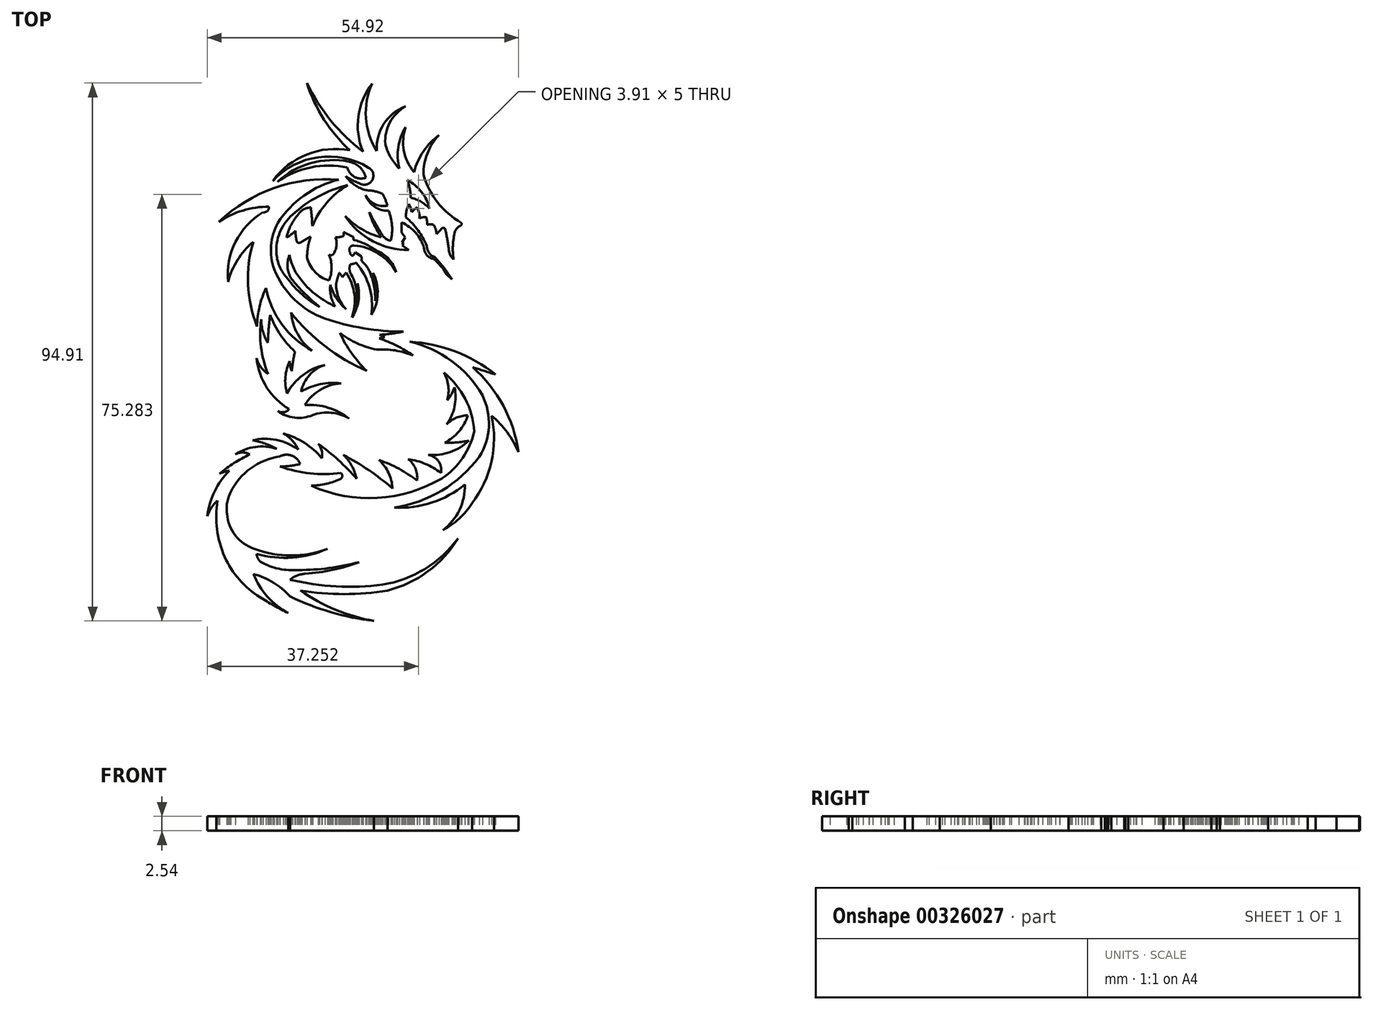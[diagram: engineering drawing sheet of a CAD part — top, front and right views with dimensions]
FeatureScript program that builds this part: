
annotation { "Feature Type Name" : "Feature", "Feature Type Description" : "" }
export const myFeature = defineFeature(function(context is Context, id is Id, definition is map)
    precondition{}
    {
        {
            var Q0;
            Q0=qCreatedBy(makeId("Top.planeOp"),FACE);
            var sketch = newSketch(context, id + "F0", { "sketchPlane" : qUnion([Q0])});
            skArc(sketch, "E0", {"start": v(-30.65, 39.22) * mm, "mid": v(-28.15, 34.33) * mm, "end": v(-23.98, 30.75) * mm});
            skArc(sketch, "E1", {"start": v(-27.91, 46.24) * mm, "mid": v(-29.97, 43) * mm, "end": v(-30.65, 39.22) * mm});
            skArc(sketch, "E2", {"start": v(-27.91, 46.24) * mm, "mid": v(-30.67, 43.35) * mm, "end": v(-32.32, 39.7) * mm});
            skArc(sketch, "E3", {"start": v(-33.8, 47.63) * mm, "mid": v(-34.11, 43.47) * mm, "end": v(-32.32, 39.7) * mm});
            skArc(sketch, "E4", {"start": v(-33.8, 47.63) * mm, "mid": v(-35.12, 44.08) * mm, "end": v(-34.92, 40.3) * mm});
            skArc(sketch, "E5", {"start": v(-37.4, 44.6) * mm, "mid": v(-36.44, 42.3) * mm, "end": v(-34.92, 40.3) * mm});
            skArc(sketch, "E6", {"start": v(-33.82, 51.28) * mm, "mid": v(-36.58, 48.47) * mm, "end": v(-37.4, 44.6) * mm});
            skArc(sketch, "E7", {"start": v(-33.82, 51.28) * mm, "mid": v(-37.67, 48.18) * mm, "end": v(-38.9, 43.4) * mm});
            skArc(sketch, "E8", {"start": v(-39.73, 55.3) * mm, "mid": v(-40.83, 49.25) * mm, "end": v(-38.9, 43.4) * mm});
            skArc(sketch, "E9", {"start": v(-39.73, 55.3) * mm, "mid": v(-42.15, 49.52) * mm, "end": v(-41.34, 43.3) * mm});
            skArc(sketch, "E10", {"start": v(-51.25, 55.4) * mm, "mid": v(-47, 48.77) * mm, "end": v(-41.34, 43.3) * mm});
            skArc(sketch, "E11", {"start": v(-51.25, 55.4) * mm, "mid": v(-48.2, 48.97) * mm, "end": v(-43.64, 43.52) * mm});
            skArc(sketch, "E12", {"start": v(-43.64, 43.52) * mm, "mid": v(-51.25, 42.81) * mm, "end": v(-57.28, 38.12) * mm});
            skArc(sketch, "E13", {"start": v(-40.35, 40.47) * mm, "mid": v(-49.23, 42.31) * mm, "end": v(-57.28, 38.12) * mm});
            skArc(sketch, "E14", {"start": v(-41.33, 37.48) * mm, "mid": v(-39.58, 38.56) * mm, "end": v(-40.35, 40.47) * mm});
            skArc(sketch, "E15", {"start": v(-44.38, 38.98) * mm, "mid": v(-42.91, 38.11) * mm, "end": v(-41.33, 37.48) * mm});
            skArc(sketch, "E16", {"start": v(-44.38, 38.98) * mm, "mid": v(-42.8, 37.4) * mm, "end": v(-40.77, 36.48) * mm});
            skArc(sketch, "E17", {"start": v(-37.91, 35.86) * mm, "mid": v(-39.31, 36.3) * mm, "end": v(-40.77, 36.48) * mm});
            skArc(sketch, "E18", {"start": v(-37.01, 33.75) * mm, "mid": v(-37.4, 34.83) * mm, "end": v(-37.91, 35.86) * mm});
            skArc(sketch, "E19", {"start": v(-40.85, 35.6) * mm, "mid": v(-39.24, 34.04) * mm, "end": v(-37.01, 33.75) * mm});
            skArc(sketch, "E20", {"start": v(-40.85, 35.6) * mm, "mid": v(-39.3, 33.56) * mm, "end": v(-36.83, 32.89) * mm});
            skArc(sketch, "E21", {"start": v(-44.1, 40.51) * mm, "mid": v(-50.54, 40.52) * mm, "end": v(-56.45, 37.97) * mm});
            skArc(sketch, "E22", {"start": v(-44.1, 40.51) * mm, "mid": v(-42.88, 38.87) * mm, "end": v(-40.83, 38.7) * mm});
            skArc(sketch, "E23", {"start": v(-40.83, 38.7) * mm, "mid": v(-41.92, 40.55) * mm, "end": v(-43.82, 41.54) * mm});
            skArc(sketch, "E24", {"start": v(-43.82, 41.54) * mm, "mid": v(-50.56, 41.26) * mm, "end": v(-56.45, 37.97) * mm});
            skArc(sketch, "E25", {"start": v(-36.45, 27.58) * mm, "mid": v(-36.2, 30.27) * mm, "end": v(-36.83, 32.89) * mm});
            skArc(sketch, "E26", {"start": v(-37.87, 28.52) * mm, "mid": v(-37.26, 27.9) * mm, "end": v(-36.45, 27.58) * mm});
            skArc(sketch, "E27", {"start": v(-40.23, 32.6) * mm, "mid": v(-39.08, 30.55) * mm, "end": v(-37.87, 28.52) * mm});
            skArc(sketch, "E28", {"start": v(-40.23, 32.6) * mm, "mid": v(-39.32, 30.32) * mm, "end": v(-38.12, 28.17) * mm});
            skArc(sketch, "E29", {"start": v(-44.48, 31.94) * mm, "mid": v(-41.56, 29.61) * mm, "end": v(-38.12, 28.17) * mm});
            skArc(sketch, "E30", {"start": v(-44.48, 31.94) * mm, "mid": v(-39.63, 27.52) * mm, "end": v(-33.25, 25.95) * mm});
            skLineSegment(sketch, "E31", {"start": v(-33.25, 25.95) * mm, "end": v(-34.39, 26.7) * mm});
            skLineSegment(sketch, "E32", {"start": v(-34.39, 26.7) * mm, "end": v(-34.17, 27.04) * mm});
            skLineSegment(sketch, "E33", {"start": v(-34.17, 27.04) * mm, "end": v(-34.49, 27.25) * mm});
            skLineSegment(sketch, "E34", {"start": v(-34.49, 27.25) * mm, "end": v(-33.88, 28.16) * mm});
            skLineSegment(sketch, "E35", {"start": v(-33.88, 28.16) * mm, "end": v(-34.5, 28.99) * mm});
            skLineSegment(sketch, "E36", {"start": v(-34.5, 28.99) * mm, "end": v(-34.5, 30.8) * mm});
            skArc(sketch, "E37", {"start": v(-30.56, 26.27) * mm, "mid": v(-32.03, 28.98) * mm, "end": v(-34.5, 30.8) * mm});
            skArc(sketch, "E38", {"start": v(-30.56, 26.27) * mm, "mid": v(-30.05, 25.03) * mm, "end": v(-28.88, 24.37) * mm});
            skArc(sketch, "E39", {"start": v(-26.66, 21.73) * mm, "mid": v(-27.64, 23.16) * mm, "end": v(-28.88, 24.37) * mm});
            skLineSegment(sketch, "E40", {"start": v(-26.66, 21.73) * mm, "end": v(-25.6, 20.73) * mm});
            skArc(sketch, "E41", {"start": v(-25.6, 20.73) * mm, "mid": v(-27.04, 22.77) * mm, "end": v(-28.66, 24.67) * mm});
            skArc(sketch, "E42", {"start": v(-30.06, 26.64) * mm, "mid": v(-29.68, 25.43) * mm, "end": v(-28.66, 24.67) * mm});
            skArc(sketch, "E43", {"start": v(-30.06, 26.64) * mm, "mid": v(-31.62, 29.41) * mm, "end": v(-33.8, 31.73) * mm});
            skArc(sketch, "E44", {"start": v(-33.24, 34.08) * mm, "mid": v(-33.64, 32.93) * mm, "end": v(-33.8, 31.73) * mm});
            skArc(sketch, "E45", {"start": v(-32.75, 32.61) * mm, "mid": v(-32.92, 33.37) * mm, "end": v(-33.24, 34.08) * mm});
            skArc(sketch, "E46", {"start": v(-31.8, 33.49) * mm, "mid": v(-32.29, 33.06) * mm, "end": v(-32.75, 32.61) * mm});
            skArc(sketch, "E47", {"start": v(-31.35, 31.52) * mm, "mid": v(-31.44, 32.54) * mm, "end": v(-31.8, 33.49) * mm});
            skArc(sketch, "E48", {"start": v(-30.2, 31.73) * mm, "mid": v(-30.8, 31.7) * mm, "end": v(-31.35, 31.52) * mm});
            skArc(sketch, "E49", {"start": v(-30.04, 30.38) * mm, "mid": v(-30.04, 31.07) * mm, "end": v(-30.2, 31.73) * mm});
            skArc(sketch, "E50", {"start": v(-28.88, 30.38) * mm, "mid": v(-29.46, 30.48) * mm, "end": v(-30.04, 30.38) * mm});
            skArc(sketch, "E51", {"start": v(-28.37, 28.76) * mm, "mid": v(-28.5, 29.61) * mm, "end": v(-28.88, 30.38) * mm});
            skArc(sketch, "E52", {"start": v(-28.37, 28.76) * mm, "mid": v(-27.87, 29.27) * mm, "end": v(-27.38, 29.8) * mm});
            skArc(sketch, "E53", {"start": v(-26.81, 29.56) * mm, "mid": v(-27.04, 29.83) * mm, "end": v(-27.38, 29.8) * mm});
            skArc(sketch, "E54", {"start": v(-26.23, 26.32) * mm, "mid": v(-26.48, 27.95) * mm, "end": v(-26.81, 29.56) * mm});
            skArc(sketch, "E55", {"start": v(-26.23, 26.32) * mm, "mid": v(-25.99, 25.22) * mm, "end": v(-25.35, 24.28) * mm});
            skArc(sketch, "E56", {"start": v(-25.1, 29.19) * mm, "mid": v(-25.46, 26.74) * mm, "end": v(-25.35, 24.28) * mm});
            skArc(sketch, "E57", {"start": v(-24.27, 30.17) * mm, "mid": v(-24.76, 29.74) * mm, "end": v(-25.1, 29.19) * mm});
            skArc(sketch, "E58", {"start": v(-24.27, 30.17) * mm, "mid": v(-23.97, 30.38) * mm, "end": v(-23.98, 30.75) * mm});
            skArc(sketch, "E59", {"start": v(-29.6, 33.27) * mm, "mid": v(-31.01, 36.2) * mm, "end": v(-33.51, 38.27) * mm});
            skArc(sketch, "E60", {"start": v(-29.6, 33.27) * mm, "mid": v(-31.1, 34.46) * mm, "end": v(-32.9, 35.15) * mm});
            skArc(sketch, "E61", {"start": v(-32.9, 35.15) * mm, "mid": v(-33.08, 36.73) * mm, "end": v(-33.51, 38.27) * mm});
            skArc(sketch, "E62", {"start": v(-44.07, 37.38) * mm, "mid": v(-49.23, 35.39) * mm, "end": v(-53.76, 32.2) * mm});
            skArc(sketch, "E63", {"start": v(-53.76, 32.2) * mm, "mid": v(-56.03, 29.04) * mm, "end": v(-56.6, 25.2) * mm});
            skArc(sketch, "E64", {"start": v(-56.6, 25.2) * mm, "mid": v(-55.99, 22.86) * mm, "end": v(-54.62, 20.88) * mm});
            skArc(sketch, "E65", {"start": v(-54.62, 20.88) * mm, "mid": v(-52.08, 18.07) * mm, "end": v(-48.97, 15.88) * mm});
            skArc(sketch, "E66", {"start": v(-54, 20.88) * mm, "mid": v(-51.62, 18.24) * mm, "end": v(-48.97, 15.88) * mm});
            skArc(sketch, "E67", {"start": v(-54.31, 25.05) * mm, "mid": v(-54.65, 22.93) * mm, "end": v(-54, 20.88) * mm});
            skArc(sketch, "E68", {"start": v(-54.31, 25.05) * mm, "mid": v(-53.52, 22.62) * mm, "end": v(-52.11, 20.49) * mm});
            skArc(sketch, "E69", {"start": v(-52.11, 20.49) * mm, "mid": v(-49.47, 17.9) * mm, "end": v(-46.27, 16.02) * mm});
            skArc(sketch, "E70", {"start": v(-47.1, 19.82) * mm, "mid": v(-47, 17.85) * mm, "end": v(-46.27, 16.02) * mm});
            skArc(sketch, "E71", {"start": v(-47.1, 19.82) * mm, "mid": v(-46.04, 17.46) * mm, "end": v(-44.33, 15.5) * mm});
            skArc(sketch, "E72", {"start": v(-46.1, 19.91) * mm, "mid": v(-45.63, 17.54) * mm, "end": v(-44.33, 15.5) * mm});
            skArc(sketch, "E73", {"start": v(-45.5, 21.93) * mm, "mid": v(-45.84, 20.93) * mm, "end": v(-46.1, 19.91) * mm});
            skArc(sketch, "E74", {"start": v(-44.98, 21.14) * mm, "mid": v(-45.23, 21.55) * mm, "end": v(-45.5, 21.93) * mm});
            skArc(sketch, "E75", {"start": v(-44.98, 21.14) * mm, "mid": v(-44.66, 21.54) * mm, "end": v(-44.33, 21.95) * mm});
            skArc(sketch, "E76", {"start": v(-43.3, 14) * mm, "mid": v(-42.86, 18.1) * mm, "end": v(-44.33, 21.95) * mm});
            skArc(sketch, "E77", {"start": v(-43.3, 14) * mm, "mid": v(-42.16, 16.91) * mm, "end": v(-42.28, 20.03) * mm});
            skArc(sketch, "E78", {"start": v(-42.64, 15.93) * mm, "mid": v(-42.28, 17.96) * mm, "end": v(-42.28, 20.03) * mm});
            skArc(sketch, "E79", {"start": v(-42.64, 15.93) * mm, "mid": v(-42.54, 19.02) * mm, "end": v(-43.58, 21.94) * mm});
            skArc(sketch, "E80", {"start": v(-43.58, 23.4) * mm, "mid": v(-43.71, 22.67) * mm, "end": v(-43.58, 21.94) * mm});
            skArc(sketch, "E81", {"start": v(-43.58, 23.4) * mm, "mid": v(-43.03, 23.5) * mm, "end": v(-42.5, 23.67) * mm});
            skArc(sketch, "E82", {"start": v(-39.85, 14.5) * mm, "mid": v(-40.19, 19.38) * mm, "end": v(-42.5, 23.67) * mm});
            skArc(sketch, "E83", {"start": v(-39.85, 14.5) * mm, "mid": v(-38.74, 18.16) * mm, "end": v(-39.58, 21.89) * mm});
            skArc(sketch, "E84", {"start": v(-39.2, 16.94) * mm, "mid": v(-39.09, 19.44) * mm, "end": v(-39.58, 21.89) * mm});
            skArc(sketch, "E85", {"start": v(-39.2, 16.94) * mm, "mid": v(-39.33, 19.35) * mm, "end": v(-40, 21.67) * mm});
            skArc(sketch, "E86", {"start": v(-40, 21.67) * mm, "mid": v(-40.65, 22.99) * mm, "end": v(-41.64, 24.08) * mm});
            skArc(sketch, "E87", {"start": v(-41.64, 24.08) * mm, "mid": v(-41.58, 24.45) * mm, "end": v(-41.64, 24.8) * mm});
            skLineSegment(sketch, "E88", {"start": v(-41.64, 24.8) * mm, "end": v(-42.69, 25.54) * mm});
            skLineSegment(sketch, "E89", {"start": v(-42.69, 25.54) * mm, "end": v(-43.1, 24.95) * mm});
            skArc(sketch, "E90", {"start": v(-43.61, 25.52) * mm, "mid": v(-43.5, 25.12) * mm, "end": v(-43.1, 24.95) * mm});
            skArc(sketch, "E91", {"start": v(-42.9, 26.75) * mm, "mid": v(-43.65, 26.36) * mm, "end": v(-43.61, 25.52) * mm});
            skArc(sketch, "E92", {"start": v(-35.5, 22.06) * mm, "mid": v(-38.63, 25.3) * mm, "end": v(-42.9, 26.75) * mm});
            skArc(sketch, "E93", {"start": v(-35.5, 22.06) * mm, "mid": v(-36.74, 24.3) * mm, "end": v(-38.86, 25.77) * mm});
            skArc(sketch, "E94", {"start": v(-38.86, 25.77) * mm, "mid": v(-40.86, 26.95) * mm, "end": v(-43.04, 27.76) * mm});
            skArc(sketch, "E95", {"start": v(-43.04, 27.76) * mm, "mid": v(-43.03, 28) * mm, "end": v(-43.04, 28.23) * mm});
            skArc(sketch, "E96", {"start": v(-43.04, 28.23) * mm, "mid": v(-43.9, 28.67) * mm, "end": v(-44.76, 29.1) * mm});
            skArc(sketch, "E97", {"start": v(-44.76, 28.4) * mm, "mid": v(-44.72, 28.75) * mm, "end": v(-44.76, 29.1) * mm});
            skArc(sketch, "E98", {"start": v(-46.2, 28.17) * mm, "mid": v(-45.47, 28.22) * mm, "end": v(-44.76, 28.4) * mm});
            skArc(sketch, "E99", {"start": v(-46.66, 25.12) * mm, "mid": v(-46.02, 26.58) * mm, "end": v(-46.2, 28.17) * mm});
            skArc(sketch, "E100", {"start": v(-47.34, 25.12) * mm, "mid": v(-47, 25.03) * mm, "end": v(-46.66, 25.12) * mm});
            skArc(sketch, "E101", {"start": v(-47.34, 20.54) * mm, "mid": v(-46.88, 22.83) * mm, "end": v(-47.34, 25.12) * mm});
            skArc(sketch, "E102", {"start": v(-51.2, 24.57) * mm, "mid": v(-49.8, 22.05) * mm, "end": v(-47.34, 20.54) * mm});
            skArc(sketch, "E103", {"start": v(-50.58, 28.31) * mm, "mid": v(-51.06, 26.47) * mm, "end": v(-51.2, 24.57) * mm});
            skArc(sketch, "E104", {"start": v(-50.58, 28.31) * mm, "mid": v(-51.46, 27.83) * mm, "end": v(-52.3, 27.29) * mm});
            skArc(sketch, "E105", {"start": v(-52.97, 27.29) * mm, "mid": v(-52.63, 27.2) * mm, "end": v(-52.3, 27.29) * mm});
            skArc(sketch, "E106", {"start": v(-53.23, 29.34) * mm, "mid": v(-53.2, 28.3) * mm, "end": v(-52.97, 27.29) * mm});
            skArc(sketch, "E107", {"start": v(-54.86, 28.12) * mm, "mid": v(-54.01, 28.68) * mm, "end": v(-53.23, 29.34) * mm});
            skArc(sketch, "E108", {"start": v(-52.71, 32.3) * mm, "mid": v(-54.04, 30.34) * mm, "end": v(-54.86, 28.12) * mm});
            skArc(sketch, "E109", {"start": v(-50.55, 33.43) * mm, "mid": v(-51.77, 33.13) * mm, "end": v(-52.71, 32.3) * mm});
            skArc(sketch, "E110", {"start": v(-50.3, 30.15) * mm, "mid": v(-50.38, 31.8) * mm, "end": v(-50.55, 33.43) * mm});
            skArc(sketch, "E111", {"start": v(-44.07, 37.38) * mm, "mid": v(-47.76, 34.26) * mm, "end": v(-50.3, 30.15) * mm});
            skArc(sketch, "E112", {"start": v(-45.67, 38.36) * mm, "mid": v(-57, 36.87) * mm, "end": v(-66.77, 30.92) * mm});
            skArc(sketch, "E113", {"start": v(-57.94, 33.58) * mm, "mid": v(-62.55, 32.91) * mm, "end": v(-66.77, 30.92) * mm});
            skArc(sketch, "E114", {"start": v(-58.97, 32.6) * mm, "mid": v(-58.21, 32.83) * mm, "end": v(-57.94, 33.58) * mm});
            skArc(sketch, "E115", {"start": v(-58.97, 32.6) * mm, "mid": v(-63.84, 27.36) * mm, "end": v(-65.15, 20.33) * mm});
            skArc(sketch, "E116", {"start": v(-60.7, 27.37) * mm, "mid": v(-63.48, 24.2) * mm, "end": v(-65.15, 20.33) * mm});
            skArc(sketch, "E117", {"start": v(-60.7, 27.37) * mm, "mid": v(-61.63, 19.86) * mm, "end": v(-60.06, 12.47) * mm});
            skArc(sketch, "E118", {"start": v(-58.46, 19.2) * mm, "mid": v(-59.6, 15.92) * mm, "end": v(-60.06, 12.47) * mm});
            skArc(sketch, "E119", {"start": v(-58.46, 19.2) * mm, "mid": v(-55.63, 12.78) * mm, "end": v(-50.33, 8.17) * mm});
            skArc(sketch, "E120", {"start": v(-54.03, 14.88) * mm, "mid": v(-52.9, 11.13) * mm, "end": v(-50.33, 8.17) * mm});
            skArc(sketch, "E121", {"start": v(-54.03, 14.88) * mm, "mid": v(-47.99, 8.91) * mm, "end": v(-40.67, 4.6) * mm});
            skArc(sketch, "E122", {"start": v(-45.41, 11.31) * mm, "mid": v(-43.35, 7.73) * mm, "end": v(-40.67, 4.6) * mm});
            skArc(sketch, "E123", {"start": v(-45.41, 11.31) * mm, "mid": v(-42.34, 9.47) * mm, "end": v(-38.93, 8.37) * mm});
            skArc(sketch, "E124", {"start": v(-32.51, 7.36) * mm, "mid": v(-35.67, 8.22) * mm, "end": v(-38.93, 8.37) * mm});
            skArc(sketch, "E125", {"start": v(-32.51, 7.36) * mm, "mid": v(-35.4, 9.06) * mm, "end": v(-38.47, 10.37) * mm});
            skLineSegment(sketch, "E126", {"start": v(-38.47, 10.37) * mm, "end": v(-37.48, 10.6) * mm});
            skLineSegment(sketch, "E127", {"start": v(-37.48, 10.6) * mm, "end": v(-38.38, 11) * mm});
            skArc(sketch, "E128", {"start": v(-38.38, 11) * mm, "mid": v(-36.3, 11.18) * mm, "end": v(-34.23, 11.53) * mm});
            skArc(sketch, "E129", {"start": v(-48.05, 13.84) * mm, "mid": v(-41.23, 12.13) * mm, "end": v(-34.23, 11.53) * mm});
            skArc(sketch, "E130", {"start": v(-57, 22.54) * mm, "mid": v(-53.46, 17.23) * mm, "end": v(-48.05, 13.84) * mm});
            skArc(sketch, "E131", {"start": v(-56.38, 30.7) * mm, "mid": v(-57.55, 26.69) * mm, "end": v(-57, 22.54) * mm});
            skArc(sketch, "E132", {"start": v(-45.67, 38.36) * mm, "mid": v(-51.74, 35.54) * mm, "end": v(-56.38, 30.7) * mm});
            skArc(sketch, "E133", {"start": v(-17.96, 3.97) * mm, "mid": v(-25.06, 8.04) * mm, "end": v(-33.07, 9.75) * mm});
            skArc(sketch, "E134", {"start": v(-17.96, 3.97) * mm, "mid": v(-19.96, 4.61) * mm, "end": v(-21.97, 5.23) * mm});
            skArc(sketch, "E135", {"start": v(-20.26, 0.3) * mm, "mid": v(-25.68, 6.35) * mm, "end": v(-33.07, 9.75) * mm});
            skArc(sketch, "E136", {"start": v(-20.8, -10.55) * mm, "mid": v(-19.11, -5.2) * mm, "end": v(-20.26, 0.3) * mm});
            skArc(sketch, "E137", {"start": v(-35.76, -19.51) * mm, "mid": v(-27.4, -16.51) * mm, "end": v(-20.8, -10.55) * mm});
            skArc(sketch, "E138", {"start": v(-35.76, -19.51) * mm, "mid": v(-29.16, -18.64) * mm, "end": v(-23.34, -15.42) * mm});
            skArc(sketch, "E139", {"start": v(-27.24, -23.5) * mm, "mid": v(-24.3, -19.93) * mm, "end": v(-23.34, -15.42) * mm});
            skArc(sketch, "E140", {"start": v(-27.24, -23.5) * mm, "mid": v(-24.36, -21.45) * mm, "end": v(-22.08, -18.75) * mm});
            skArc(sketch, "E141", {"start": v(-22.08, -18.75) * mm, "mid": v(-18.67, -11.4) * mm, "end": v(-18.62, -3.3) * mm});
            skArc(sketch, "E142", {"start": v(-13.89, -9.75) * mm, "mid": v(-15.88, -6.25) * mm, "end": v(-18.62, -3.3) * mm});
            skArc(sketch, "E143", {"start": v(-13.89, -9.75) * mm, "mid": v(-16.57, -1.53) * mm, "end": v(-21.97, 5.23) * mm});
            skArc(sketch, "E144", {"start": v(-21.7, -6.08) * mm, "mid": v(-23.29, -0.33) * mm, "end": v(-27.05, 4.3) * mm});
            skArc(sketch, "E145", {"start": v(-27.38, -14.33) * mm, "mid": v(-23.73, -10.76) * mm, "end": v(-21.7, -6.08) * mm});
            skArc(sketch, "E146", {"start": v(-50.47, -15.66) * mm, "mid": v(-38.76, -17.81) * mm, "end": v(-27.38, -14.33) * mm});
            skArc(sketch, "E147", {"start": v(-50.47, -15.66) * mm, "mid": v(-47.78, -15.3) * mm, "end": v(-45.2, -14.43) * mm});
            skArc(sketch, "E148", {"start": v(-45.2, -14.43) * mm, "mid": v(-45, -13.92) * mm, "end": v(-45.2, -13.42) * mm});
            skArc(sketch, "E149", {"start": v(-56.02, -12.25) * mm, "mid": v(-50.68, -13.48) * mm, "end": v(-45.2, -13.42) * mm});
            skArc(sketch, "E150", {"start": v(-56.02, -12.25) * mm, "mid": v(-54.2, -12.16) * mm, "end": v(-52.43, -11.8) * mm});
            skArc(sketch, "E151", {"start": v(-52.43, -11.8) * mm, "mid": v(-53.94, -10.34) * mm, "end": v(-56.04, -10.5) * mm});
            skArc(sketch, "E152", {"start": v(-56.04, -10.5) * mm, "mid": v(-61.13, -12.57) * mm, "end": v(-64.67, -16.8) * mm});
            skArc(sketch, "E153", {"start": v(-64.93, -13.02) * mm, "mid": v(-65.8, -13.2) * mm, "end": v(-66.63, -13.52) * mm});
            skArc(sketch, "E154", {"start": v(-61.33, -10.13) * mm, "mid": v(-64.09, -11.66) * mm, "end": v(-66.63, -13.52) * mm});
            skArc(sketch, "E155", {"start": v(-61.33, -10.13) * mm, "mid": v(-62.6, -9.8) * mm, "end": v(-63.86, -10.13) * mm});
            skArc(sketch, "E156", {"start": v(-56.58, -9.13) * mm, "mid": v(-60.33, -8.82) * mm, "end": v(-63.86, -10.13) * mm});
            skArc(sketch, "E157", {"start": v(-56.58, -9.13) * mm, "mid": v(-58.64, -8.21) * mm, "end": v(-60.84, -7.65) * mm});
            skArc(sketch, "E158", {"start": v(-52.77, -9.26) * mm, "mid": v(-56.63, -7.57) * mm, "end": v(-60.84, -7.65) * mm});
            skArc(sketch, "E159", {"start": v(-52.77, -9.26) * mm, "mid": v(-53.86, -7.63) * mm, "end": v(-55.42, -6.45) * mm});
            skArc(sketch, "E160", {"start": v(-48.6, -10.83) * mm, "mid": v(-51.66, -8.1) * mm, "end": v(-55.42, -6.45) * mm});
            skArc(sketch, "E161", {"start": v(-48.6, -10.83) * mm, "mid": v(-48.62, -9.47) * mm, "end": v(-49.25, -8.26) * mm});
            skArc(sketch, "E162", {"start": v(-42.47, -14.43) * mm, "mid": v(-45.68, -11.15) * mm, "end": v(-49.25, -8.26) * mm});
            skArc(sketch, "E163", {"start": v(-42.47, -14.43) * mm, "mid": v(-43.32, -12.15) * mm, "end": v(-44.78, -10.2) * mm});
            skArc(sketch, "E164", {"start": v(-36.14, -16.12) * mm, "mid": v(-40.3, -12.92) * mm, "end": v(-44.78, -10.2) * mm});
            skArc(sketch, "E165", {"start": v(-36.14, -16.12) * mm, "mid": v(-36.82, -13.4) * mm, "end": v(-38.5, -11.15) * mm});
            skArc(sketch, "E166", {"start": v(-31.8, -14.75) * mm, "mid": v(-35, -12.67) * mm, "end": v(-38.5, -11.15) * mm});
            skArc(sketch, "E167", {"start": v(-31.8, -14.75) * mm, "mid": v(-32.07, -12.65) * mm, "end": v(-33.36, -10.98) * mm});
            skArc(sketch, "E168", {"start": v(-27.57, -13.42) * mm, "mid": v(-30.3, -11.81) * mm, "end": v(-33.36, -10.98) * mm});
            skArc(sketch, "E169", {"start": v(-27.57, -13.42) * mm, "mid": v(-28, -11.34) * mm, "end": v(-29.8, -10.23) * mm});
            skArc(sketch, "E170", {"start": v(-26.9, -8.08) * mm, "mid": v(-24.76, -8.02) * mm, "end": v(-22.64, -7.7) * mm});
            skArc(sketch, "E171", {"start": v(-26.9, -8.08) * mm, "mid": v(-24.38, -6.06) * mm, "end": v(-22.81, -3.23) * mm});
            skArc(sketch, "E172", {"start": v(-22.81, -3.23) * mm, "mid": v(-24.84, -3.66) * mm, "end": v(-26.58, -4.8) * mm});
            skArc(sketch, "E173", {"start": v(-29.8, -10.23) * mm, "mid": v(-25.95, -9.73) * mm, "end": v(-22.64, -7.7) * mm});
            skArc(sketch, "E174", {"start": v(-26.58, -4.8) * mm, "mid": v(-25.17, -1.7) * mm, "end": v(-25.17, 1.7) * mm});
            skArc(sketch, "E175", {"start": v(-26.45, -0.58) * mm, "mid": v(-25.71, 0.5) * mm, "end": v(-25.17, 1.7) * mm});
            skArc(sketch, "E176", {"start": v(-26.45, -0.58) * mm, "mid": v(-26.27, 1.92) * mm, "end": v(-27.05, 4.3) * mm});
            skArc(sketch, "E177", {"start": v(-57.73, 14.46) * mm, "mid": v(-55.92, 10.98) * mm, "end": v(-53.36, 8) * mm});
            skArc(sketch, "E178", {"start": v(-53.36, 8) * mm, "mid": v(-53.68, 6.3) * mm, "end": v(-53.92, 4.56) * mm});
            skArc(sketch, "E179", {"start": v(-54.26, 6.36) * mm, "mid": v(-54.17, 5.45) * mm, "end": v(-53.92, 4.56) * mm});
            skArc(sketch, "E180", {"start": v(-54.26, 6.36) * mm, "mid": v(-55.04, 3.55) * mm, "end": v(-54.77, 0.65) * mm});
            skArc(sketch, "E181", {"start": v(-57.73, 14.46) * mm, "mid": v(-58, 12.01) * mm, "end": v(-58.13, 9.56) * mm});
            skArc(sketch, "E182", {"start": v(-59.31, 13.7) * mm, "mid": v(-59, 11.55) * mm, "end": v(-58.13, 9.56) * mm});
            skArc(sketch, "E183", {"start": v(-59.31, 13.7) * mm, "mid": v(-59.34, 8.8) * mm, "end": v(-58.1, 4.06) * mm});
            skArc(sketch, "E184", {"start": v(-60.11, 6.84) * mm, "mid": v(-59.35, 5.27) * mm, "end": v(-58.1, 4.06) * mm});
            skArc(sketch, "E185", {"start": v(-60.11, 6.84) * mm, "mid": v(-58.3, 1.67) * mm, "end": v(-54.37, -2.13) * mm});
            skArc(sketch, "E186", {"start": v(-56.39, -2.48) * mm, "mid": v(-55.31, -2.69) * mm, "end": v(-54.37, -2.13) * mm});
            skArc(sketch, "E187", {"start": v(-56.39, -2.48) * mm, "mid": v(-53.4, -3.64) * mm, "end": v(-50.23, -3.2) * mm});
            skArc(sketch, "E188", {"start": v(-43.8, -3.8) * mm, "mid": v(-46.94, -2.78) * mm, "end": v(-50.23, -3.2) * mm});
            skArc(sketch, "E189", {"start": v(-43.8, -3.8) * mm, "mid": v(-47.47, -1.89) * mm, "end": v(-51.58, -1.4) * mm});
            skArc(sketch, "E190", {"start": v(-45.22, 2.4) * mm, "mid": v(-48.87, 1.28) * mm, "end": v(-51.58, -1.4) * mm});
            skArc(sketch, "E191", {"start": v(-45.22, 2.4) * mm, "mid": v(-48.85, 2.26) * mm, "end": v(-52.25, 0.97) * mm});
            skArc(sketch, "E192", {"start": v(-48.04, 5.67) * mm, "mid": v(-50.78, 3.89) * mm, "end": v(-52.25, 0.97) * mm});
            skArc(sketch, "E193", {"start": v(-48.04, 5.67) * mm, "mid": v(-51.93, 3.88) * mm, "end": v(-54.77, 0.65) * mm});
            skArc(sketch, "E194", {"start": v(-64.93, -13.02) * mm, "mid": v(-67.55, -16.69) * mm, "end": v(-68.81, -21) * mm});
            skArc(sketch, "E195", {"start": v(-67, -18.3) * mm, "mid": v(-68.09, -19.53) * mm, "end": v(-68.81, -21) * mm});
            skArc(sketch, "E196", {"start": v(-67, -18.3) * mm, "mid": v(-67.1, -23.34) * mm, "end": v(-65.75, -28.2) * mm});
            skArc(sketch, "E197", {"start": v(-65.75, -28.2) * mm, "mid": v(-63.17, -32.24) * mm, "end": v(-59.52, -35.34) * mm});
            skArc(sketch, "E198", {"start": v(-59.52, -35.34) * mm, "mid": v(-57.05, -36.8) * mm, "end": v(-54.52, -38.12) * mm});
            skArc(sketch, "E199", {"start": v(-60.67, -31.23) * mm, "mid": v(-58.2, -35.23) * mm, "end": v(-54.52, -38.12) * mm});
            skArc(sketch, "E200", {"start": v(-54.2, -35.2) * mm, "mid": v(-57.15, -32.75) * mm, "end": v(-60.67, -31.23) * mm});
            skArc(sketch, "E201", {"start": v(-54.2, -35.2) * mm, "mid": v(-47, -37.98) * mm, "end": v(-39.42, -39.51) * mm});
            skArc(sketch, "E202", {"start": v(-52.36, -34.16) * mm, "mid": v(-46.18, -37.54) * mm, "end": v(-39.42, -39.51) * mm});
            skArc(sketch, "E203", {"start": v(-52.36, -34.16) * mm, "mid": v(-44.67, -34.79) * mm, "end": v(-36.98, -34.16) * mm});
            skArc(sketch, "E204", {"start": v(-36.98, -34.16) * mm, "mid": v(-29.87, -30.77) * mm, "end": v(-24.56, -24.94) * mm});
            skArc(sketch, "E205", {"start": v(-37.85, -33.11) * mm, "mid": v(-30.4, -30.33) * mm, "end": v(-24.56, -24.94) * mm});
            skArc(sketch, "E206", {"start": v(-54.2, -32.24) * mm, "mid": v(-46.07, -33.43) * mm, "end": v(-37.85, -33.11) * mm});
            skArc(sketch, "E207", {"start": v(-51.52, -31.2) * mm, "mid": v(-52.95, -31.5) * mm, "end": v(-54.2, -32.24) * mm});
            skArc(sketch, "E208", {"start": v(-51.52, -31.2) * mm, "mid": v(-46.7, -30.52) * mm, "end": v(-42.03, -29.15) * mm});
            skArc(sketch, "E209", {"start": v(-52.7, -30.54) * mm, "mid": v(-47.32, -30.2) * mm, "end": v(-42.03, -29.15) * mm});
            skArc(sketch, "E210", {"start": v(-59.42, -29.11) * mm, "mid": v(-56.17, -30.31) * mm, "end": v(-52.7, -30.54) * mm});
            skArc(sketch, "E211", {"start": v(-60.12, -27.72) * mm, "mid": v(-59.89, -28.48) * mm, "end": v(-59.42, -29.11) * mm});
            skArc(sketch, "E212", {"start": v(-60.12, -27.72) * mm, "mid": v(-53.77, -28.33) * mm, "end": v(-47.6, -26.78) * mm});
            skArc(sketch, "E213", {"start": v(-60.5, -26.78) * mm, "mid": v(-54.05, -27.97) * mm, "end": v(-47.6, -26.78) * mm});
            skArc(sketch, "E214", {"start": v(-65.33, -20.62) * mm, "mid": v(-63.86, -24.44) * mm, "end": v(-60.5, -26.78) * mm});
            skArc(sketch, "E215", {"start": v(-64.67, -16.8) * mm, "mid": v(-65.32, -18.65) * mm, "end": v(-65.33, -20.62) * mm});
            skSolve(sketch);
        }
        {
            var Q0;
            Q0=qSketchRegion(id+"F0",true);
            extrude(context, id + "F1", {"entities" : qUnion([Q0]), "depth" : 2.54 * mm});
        }
    });
